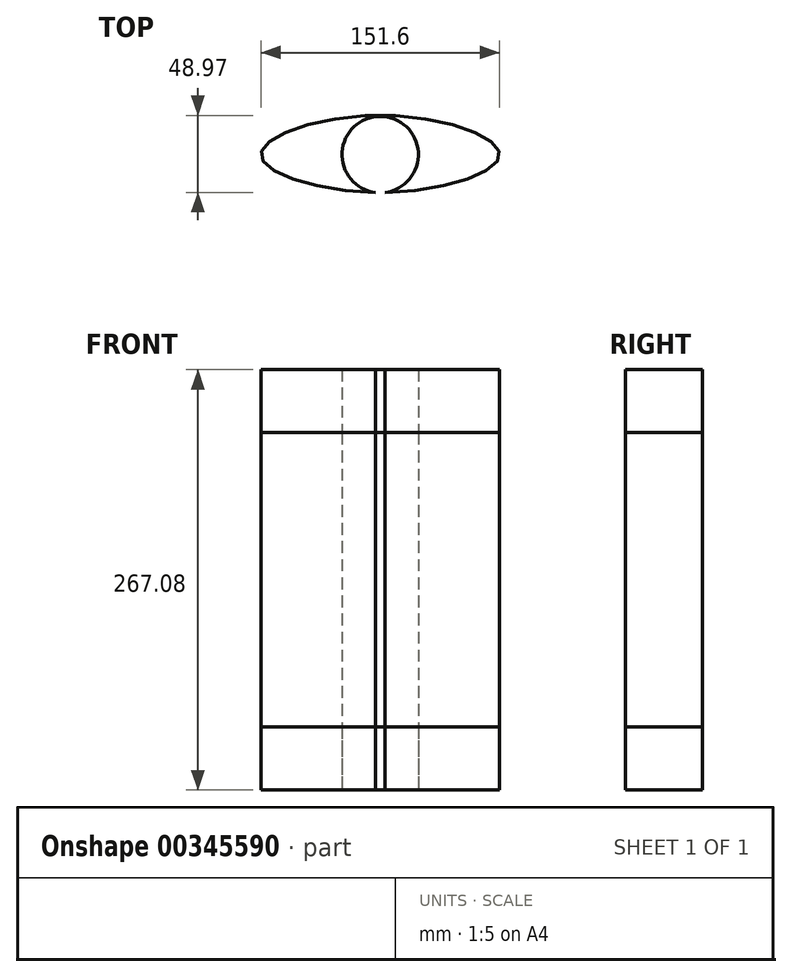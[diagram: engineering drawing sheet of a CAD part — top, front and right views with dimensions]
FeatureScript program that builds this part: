
annotation { "Feature Type Name" : "Feature", "Feature Type Description" : "" }
export const myFeature = defineFeature(function(context is Context, id is Id, definition is map)
    precondition{}
    {
        {
            var Q0;
            Q0=qCreatedBy(makeId("Top.planeOp"),FACE);
            var sketch = newSketch(context, id + "F0", { "sketchPlane" : qUnion([Q0])});
            skFitSpline(sketch, "E0", {"points": [v(-75.8, 0) * mm, v(0, 24.88) * mm, v(75.8, 0) * mm, v(0, -24.12) * mm, v(-75.8, 0) * mm]});
            skCircle(sketch, "E1", {"center": v(0, 0) * mm, "radius": 24.27 * mm});
            skCircle(sketch, "E2", {"center": v(0, 0) * mm, "radius": 7.91 * mm});
            skSolve(sketch);
        }
        {
            var Q0;
            {var subQ0=sQuery(id+"F0.wireOp",EDGE,"E1");var subQ1=sQuery(id+"F0.wireOp",EDGE,"E0");var subQ2=makeQuery(id+"F0.imprint","INTERSECT",VERTEX,{"disambiguationData":[OD(0.0)],"derivedFrom":[subQ1,subQ0]});Q0=makeQuery(id+"F0.imprint","IMPRINT",FACE,{"disambiguationData":[TD([[makeQuery(id+"F0.imprint","IMPRINT",EDGE,{"disambiguationData":[TD([[subQ2,-1.0]])],"derivedFrom":subQ1}),-1.0]])]});}
            extrude(context, id + "F1", {"entities" : qUnion([Q0]), "depth" : 227.08 * mm});
        }
        {
            var Q0;
            Q0=makeQuery(id+"F1.opExtrude","CAP_FACE",FACE,{"disambiguationData":[OSD([sQuery(id+"F0.wireOp",EDGE,"E0")])],"isStart":false});
            var Q1;
            Q1=makeQuery(id+"F1.opExtrude","CAP_FACE",FACE,{"disambiguationData":[OSD([sQuery(id+"F0.wireOp",EDGE,"E0")])],"isStart":true});
            extrude(context, id + "F2", {"entities" : qUnion([Q0, Q1]), "depth" : 40 * mm});
        }
    });
